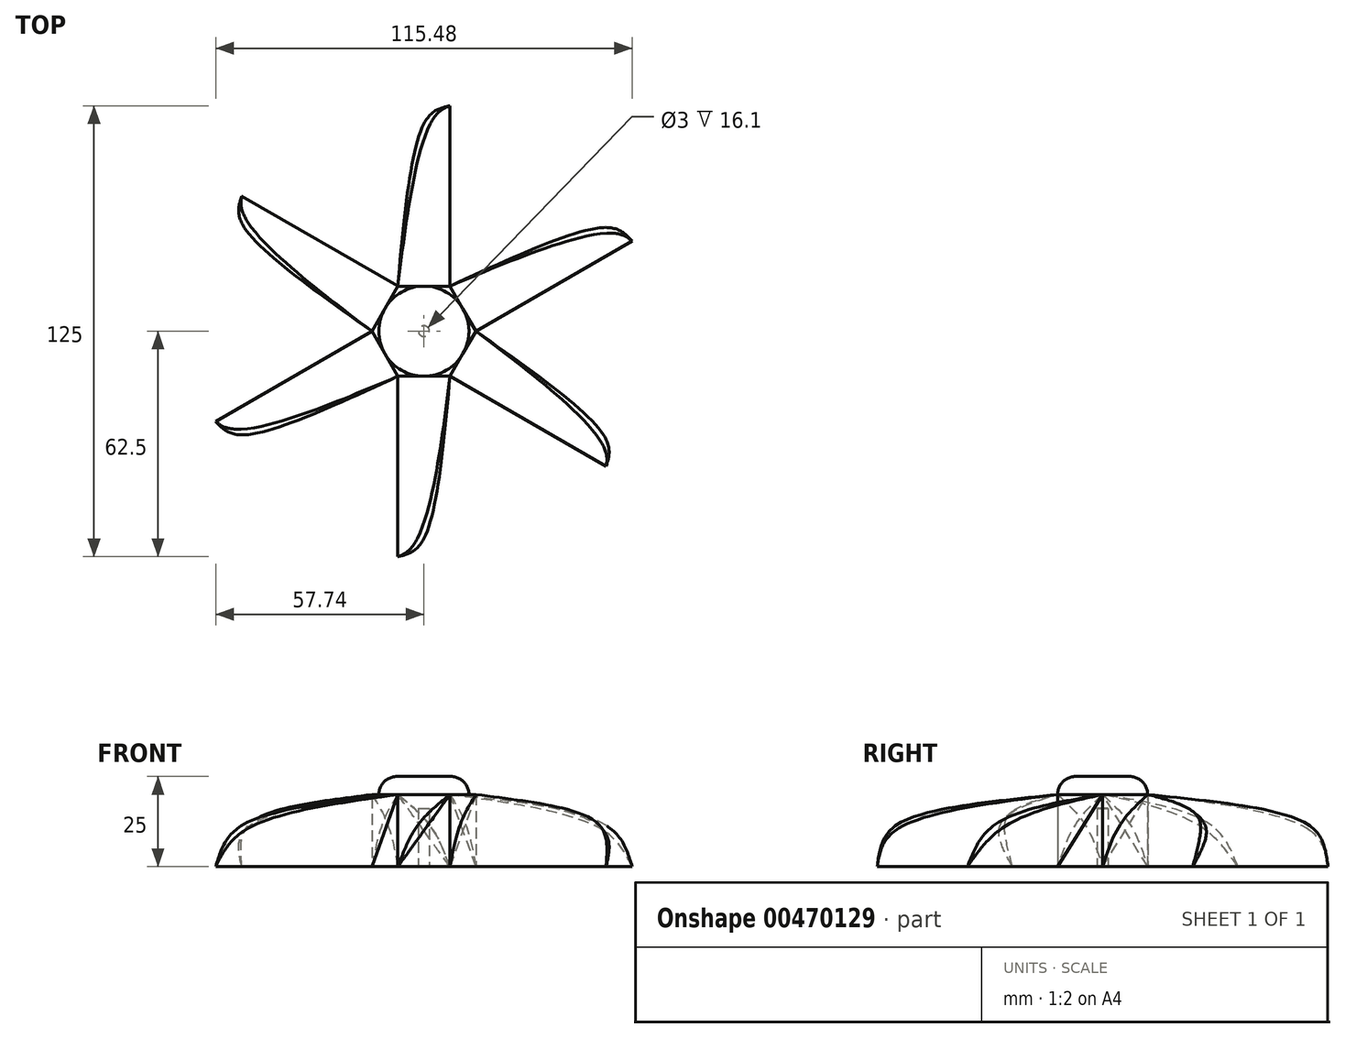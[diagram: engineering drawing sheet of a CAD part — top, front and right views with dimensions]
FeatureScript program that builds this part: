
annotation { "Feature Type Name" : "Feature", "Feature Type Description" : "" }
export const myFeature = defineFeature(function(context is Context, id is Id, definition is map)
    precondition{}
    {
        {
            var Q0;
            Q0=qCreatedBy(makeId("Top.planeOp"),FACE);
            var sketch = newSketch(context, id + "F0", { "sketchPlane" : qUnion([Q0])});
            skCircle(sketch, "E0.cCircle", {"center": v(0, 0) * mm, "radius": 12.5 * mm, "construction": true});
            skLineSegment(sketch, "E0.0", {"start": v(-14.43, 0) * mm, "end": v(-7.22, 12.5) * mm});
            skLineSegment(sketch, "E0.1", {"start": v(-7.22, 12.5) * mm, "end": v(7.22, 12.5) * mm});
            skLineSegment(sketch, "E0.2", {"start": v(7.22, 12.5) * mm, "end": v(14.43, 0) * mm});
            skLineSegment(sketch, "E0.3", {"start": v(14.43, 0) * mm, "end": v(7.22, -12.5) * mm});
            skLineSegment(sketch, "E0.4", {"start": v(7.22, -12.5) * mm, "end": v(-7.22, -12.5) * mm});
            skLineSegment(sketch, "E0.5", {"start": v(-7.22, -12.5) * mm, "end": v(-14.43, 0) * mm});
            skPoint(sketch, "E0.0.midPoint", {"position": v(-10.83, 6.25) * mm});
            skSolve(sketch);
        }
        {
            var Q0;
            Q0=makeQuery(id+"F0.imprint","IMPRINT",FACE,{"disambiguationData":[TD([[makeQuery(id+"F0.imprint","IMPRINT",EDGE,{"derivedFrom":sQuery(id+"F0.wireOp",EDGE,"E0.0")}),-1.0]])]});
            extrude(context, id + "F1", {"entities" : qUnion([Q0]), "depth" : 20 * mm});
        }
        {
            var Q0;
            Q0=makeQuery(id+"F1.opExtrude","SWEPT_FACE",FACE,{"disambiguationData":[OSD([sQuery(id+"F0.wireOp",EDGE,"E0.4")])]});
            var sketch = newSketch(context, id + "F2", { "sketchPlane" : qUnion([Q0])});
            skLineSegment(sketch, "E1", {"start": v(7.22, 20) * mm, "end": v(-7.22, 0) * mm});
            skPoint(sketch, "E2", {"position": v(0, 10) * mm});
            skLineSegment(sketch, "E3", {"start": v(0, 10) * mm, "end": v(-5.73, 14.13) * mm});
            skFitSpline(sketch, "E4", {"points": [v(7.22, 20) * mm, v(-1.82, 11.31) * mm, v(-7.22, 0) * mm], "startDerivative": vector(-19.93, -16.03) * mm, "endDerivative": vector(-8.93, -23.97) * mm});
            skSolve(sketch);
        }
        {
            var Q0;
            {var subQ1=sQuery(id+"F2.wireOp",EDGE,"E1");var subQ4=sQuery(id+"F2.wireOp",EDGE,"E3");var subQ5=makeQuery(id+"F2.imprint","INTERSECT",VERTEX,{"derivedFrom":[subQ1,subQ4]});Q0=makeQuery(id+"F2.imprint","IMPRINT",FACE,{"disambiguationData":[TD([[makeQuery(id+"F2.imprint","IMPRINT",EDGE,{"disambiguationData":[TD([[subQ5,-1.0]])],"derivedFrom":subQ4}),-1.0]])]});}
            var Q1;
            {var subQ1=sQuery(id+"F2.wireOp",EDGE,"E1");var subQ4=sQuery(id+"F2.wireOp",EDGE,"E3");var subQ5=makeQuery(id+"F2.imprint","INTERSECT",VERTEX,{"derivedFrom":[subQ1,subQ4]});Q1=makeQuery(id+"F2.imprint","IMPRINT",FACE,{"disambiguationData":[TD([[makeQuery(id+"F2.imprint","IMPRINT",EDGE,{"disambiguationData":[TD([[subQ5,-1.0]])],"derivedFrom":subQ4}),1.0]])]});}
            extrude(context, id + "F3", {"entities" : qUnion([Q0, Q1]), "operationType" : NewBodyOperationType.ADD, "depth" : 50 * mm});
        }
        {
            var Q0;
            Q0=makeQuery(id+"F1.opExtrude","SWEPT_FACE",FACE,{"disambiguationData":[OSD([sQuery(id+"F0.wireOp",EDGE,"E0.3")])]});
            var sketch = newSketch(context, id + "F4", { "sketchPlane" : qUnion([Q0])});
            skFitSpline(sketch, "E5", {"points": [v(7.22, 20) * mm, v(-1.82, 11.31) * mm, v(-7.22, 0) * mm], "startDerivative": vector(-19.93, -16.03) * mm, "endDerivative": vector(-8.93, -23.97) * mm});
            skLineSegment(sketch, "E6", {"start": v(7.22, 20) * mm, "end": v(-7.22, 0) * mm});
            skSolve(sketch);
        }
        {
            var Q0;
            Q0 = qSketchRegion(id + "F4", true);
            extrude(context, id + "F5", {"entities" : qUnion([Q0]), "operationType" : NewBodyOperationType.ADD, "depth" : 50 * mm});
        }
        {
            var Q0;
            Q0=makeQuery(id+"F1.opExtrude","SWEPT_FACE",FACE,{"disambiguationData":[OSD([sQuery(id+"F0.wireOp",EDGE,"E0.2")])]});
            var sketch = newSketch(context, id + "F6", { "sketchPlane" : qUnion([Q0])});
            skFitSpline(sketch, "E7", {"points": [v(7.22, 20) * mm, v(-1.82, 11.31) * mm, v(-7.22, 0) * mm], "startDerivative": vector(-19.93, -16.03) * mm, "endDerivative": vector(-8.93, -23.97) * mm});
            skLineSegment(sketch, "E8", {"start": v(-7.22, 0) * mm, "end": v(7.22, 20) * mm});
            skSolve(sketch);
        }
        {
            var Q0;
            Q0 = qSketchRegion(id + "F6", true);
            extrude(context, id + "F7", {"entities" : qUnion([Q0]), "operationType" : NewBodyOperationType.ADD, "depth" : 50 * mm});
        }
        {
            var Q0;
            Q0=makeQuery(id+"F1.opExtrude","SWEPT_FACE",FACE,{"disambiguationData":[OSD([sQuery(id+"F0.wireOp",EDGE,"E0.1")])]});
            var sketch = newSketch(context, id + "F8", { "sketchPlane" : qUnion([Q0])});
            skFitSpline(sketch, "E9", {"points": [v(7.25, 20) * mm, v(-1.78, 11.31) * mm, v(-7.18, 0) * mm], "startDerivative": vector(-19.93, -16.03) * mm, "endDerivative": vector(-8.93, -23.97) * mm});
            skLineSegment(sketch, "E10", {"start": v(-7.18, 0) * mm, "end": v(7.25, 20) * mm});
            skSolve(sketch);
        }
        {
            var Q0;
            Q0 = qSketchRegion(id + "F8", true);
            extrude(context, id + "F9", {"entities" : qUnion([Q0]), "operationType" : NewBodyOperationType.ADD, "depth" : 50 * mm});
        }
        {
            var Q0;
            Q0=makeQuery(id+"F1.opExtrude","SWEPT_FACE",FACE,{"disambiguationData":[OSD([sQuery(id+"F0.wireOp",EDGE,"E0.0")])]});
            var sketch = newSketch(context, id + "F10", { "sketchPlane" : qUnion([Q0])});
            skFitSpline(sketch, "E11", {"points": [v(7.22, 20) * mm, v(-1.82, 11.31) * mm, v(-7.22, 0) * mm], "startDerivative": vector(-19.93, -16.03) * mm, "endDerivative": vector(-8.93, -23.97) * mm});
            skLineSegment(sketch, "E12", {"start": v(-7.22, 0) * mm, "end": v(7.22, 20) * mm});
            skSolve(sketch);
        }
        {
            var Q0;
            Q0 = qSketchRegion(id + "F10", true);
            extrude(context, id + "F11", {"entities" : qUnion([Q0]), "operationType" : NewBodyOperationType.ADD, "depth" : 50 * mm});
        }
        {
            var Q0;
            Q0=makeQuery(id+"F1.opExtrude","SWEPT_FACE",FACE,{"disambiguationData":[OSD([sQuery(id+"F0.wireOp",EDGE,"E0.5")])]});
            var sketch = newSketch(context, id + "F12", { "sketchPlane" : qUnion([Q0])});
            skFitSpline(sketch, "E13", {"points": [v(7.22, 20) * mm, v(-1.82, 11.31) * mm, v(-7.22, 0) * mm], "startDerivative": vector(-19.93, -16.03) * mm, "endDerivative": vector(-8.93, -23.97) * mm});
            skLineSegment(sketch, "E14", {"start": v(-7.22, 0) * mm, "end": v(7.22, 20) * mm});
            skSolve(sketch);
        }
        {
            var Q0;
            Q0 = qSketchRegion(id + "F12", true);
            extrude(context, id + "F13", {"entities" : qUnion([Q0]), "operationType" : NewBodyOperationType.ADD, "depth" : 50 * mm});
        }
        {
            var Q0;
            Q0=makeQuery(id+"F13.opExtrude","SWEPT_FACE",FACE,{"disambiguationData":[OSD([sQuery(id+"F12.wireOp",EDGE,"E14")])]});
            var sketch = newSketch(context, id + "F14", { "sketchPlane" : qUnion([Q0])});
            skPoint(sketch, "E15", {"position": v(-56.62, 27.69) * mm});
            skLineSegment(sketch, "E16", {"start": v(-56.62, 27.69) * mm, "end": v(-51.88, 26.09) * mm});
            skFitSpline(sketch, "E17", {"points": [v(-60.56, 16) * mm, v(-51.88, 26.09) * mm, v(-5.3, 23.37) * mm], "startDerivative": vector(16.85, 34.73) * mm, "endDerivative": vector(86.61, -14.97) * mm});
            skSolve(sketch);
        }
        {
            var Q0;
            {var subQ0=sQuery(id+"F14.wireOp",EDGE,"E16");Q0=makeQuery(id+"F14.imprint","IMPRINT",FACE,{"disambiguationData":[TD([[makeQuery(id+"F14.imprint","IMPRINT",EDGE,{"derivedFrom":subQ0}),1.0]])]});}
            var Q1;
            {var subQ0=sQuery(id+"F14.wireOp",EDGE,"E16");Q1=makeQuery(id+"F14.imprint","IMPRINT",FACE,{"disambiguationData":[TD([[makeQuery(id+"F14.imprint","IMPRINT",EDGE,{"derivedFrom":subQ0}),-1.0]])]});}
            extrude(context, id + "F15", {"entities" : qUnion([Q0, Q1]), "operationType" : NewBodyOperationType.REMOVE, "oppositeDirection" : true, "depth" : 25 * mm});
        }
        {
            var Q0;
            Q0=makeQuery(id+"F3.opExtrude","SWEPT_FACE",FACE,{"disambiguationData":[OSD([sQuery(id+"F2.wireOp",EDGE,"E1")])]});
            var sketch = newSketch(context, id + "F16", { "sketchPlane" : qUnion([Q0])});
            skPoint(sketch, "E18", {"position": v(-62.5, 8.1) * mm});
            skLineSegment(sketch, "E19", {"start": v(-62.5, 8.1) * mm, "end": v(-57.5, 8.1) * mm});
            skFitSpline(sketch, "E20", {"points": [v(-62.5, -4.22) * mm, v(-57.5, 8.1) * mm, v(-12.5, 20.44) * mm], "startDerivative": vector(4.85, 38.3) * mm, "endDerivative": vector(86.85, 13.54) * mm});
            skSolve(sketch);
        }
        {
            var Q0;
            {var subQ0=sQuery(id+"F16.wireOp",EDGE,"E19");Q0=makeQuery(id+"F16.imprint","IMPRINT",FACE,{"disambiguationData":[TD([[makeQuery(id+"F16.imprint","IMPRINT",EDGE,{"derivedFrom":subQ0}),1.0]])]});}
            var Q1;
            {var subQ0=sQuery(id+"F16.wireOp",EDGE,"E19");Q1=makeQuery(id+"F16.imprint","IMPRINT",FACE,{"disambiguationData":[TD([[makeQuery(id+"F16.imprint","IMPRINT",EDGE,{"derivedFrom":subQ0}),-1.0]])]});}
            extrude(context, id + "F17", {"entities" : qUnion([Q0, Q1]), "operationType" : NewBodyOperationType.REMOVE, "oppositeDirection" : true, "depth" : 25 * mm});
        }
        {
            var Q0;
            Q0=makeQuery(id+"F5.opExtrude","SWEPT_FACE",FACE,{"disambiguationData":[OSD([sQuery(id+"F4.wireOp",EDGE,"E6")])]});
            var sketch = newSketch(context, id + "F18", { "sketchPlane" : qUnion([Q0])});
            skPoint(sketch, "E21", {"position": v(-61.8, -12.32) * mm});
            skLineSegment(sketch, "E22", {"start": v(-61.8, -12.32) * mm, "end": v(-57.07, -10.72) * mm});
            skFitSpline(sketch, "E23", {"points": [v(-57.86, -24) * mm, v(-57.07, -10.72) * mm, v(-18.39, 15.36) * mm], "startDerivative": vector(-7.67, 37.83) * mm, "endDerivative": vector(77.95, 40.63) * mm});
            skSolve(sketch);
        }
        {
            var Q0;
            {var subQ0=sQuery(id+"F18.wireOp",EDGE,"E22");Q0=makeQuery(id+"F18.imprint","IMPRINT",FACE,{"disambiguationData":[TD([[makeQuery(id+"F18.imprint","IMPRINT",EDGE,{"derivedFrom":subQ0}),1.0]])]});}
            var Q1;
            {var subQ0=sQuery(id+"F18.wireOp",EDGE,"E22");Q1=makeQuery(id+"F18.imprint","IMPRINT",FACE,{"disambiguationData":[TD([[makeQuery(id+"F18.imprint","IMPRINT",EDGE,{"derivedFrom":subQ0}),-1.0]])]});}
            extrude(context, id + "F19", {"entities" : qUnion([Q0, Q1]), "operationType" : NewBodyOperationType.REMOVE, "oppositeDirection" : true, "depth" : 25 * mm});
        }
        {
            var Q0;
            Q0=makeQuery(id+"F7.opExtrude","SWEPT_FACE",FACE,{"disambiguationData":[OSD([sQuery(id+"F6.wireOp",EDGE,"E8")])]});
            var sketch = newSketch(context, id + "F20", { "sketchPlane" : qUnion([Q0])});
            skPoint(sketch, "E24", {"position": v(-56.62, 27.69) * mm});
            skLineSegment(sketch, "E25", {"start": v(-56.62, 27.69) * mm, "end": v(-51.88, 26.09) * mm});
            skFitSpline(sketch, "E26", {"points": [v(-60.56, 16) * mm, v(-51.88, 26.09) * mm, v(-5.3, 23.37) * mm], "startDerivative": vector(16.85, 34.73) * mm, "endDerivative": vector(86.61, -14.97) * mm});
            skSolve(sketch);
        }
        {
            var Q0;
            {var subQ0=sQuery(id+"F20.wireOp",EDGE,"E25");Q0=makeQuery(id+"F20.imprint","IMPRINT",FACE,{"disambiguationData":[TD([[makeQuery(id+"F20.imprint","IMPRINT",EDGE,{"derivedFrom":subQ0}),1.0]])]});}
            var Q1;
            {var subQ0=sQuery(id+"F20.wireOp",EDGE,"E25");Q1=makeQuery(id+"F20.imprint","IMPRINT",FACE,{"disambiguationData":[TD([[makeQuery(id+"F20.imprint","IMPRINT",EDGE,{"derivedFrom":subQ0}),-1.0]])]});}
            extrude(context, id + "F21", {"entities" : qUnion([Q0, Q1]), "operationType" : NewBodyOperationType.REMOVE, "oppositeDirection" : true, "depth" : 25 * mm});
        }
        {
            var Q0;
            Q0=makeQuery(id+"F9.opExtrude","SWEPT_FACE",FACE,{"disambiguationData":[OSD([sQuery(id+"F8.wireOp",EDGE,"E10")])]});
            var sketch = newSketch(context, id + "F22", { "sketchPlane" : qUnion([Q0])});
            skPoint(sketch, "E27", {"position": v(-62.5, 8.13) * mm});
            skLineSegment(sketch, "E28", {"start": v(-62.5, 8.13) * mm, "end": v(-57.5, 8.13) * mm});
            skFitSpline(sketch, "E29", {"points": [v(-62.5, -4.2) * mm, v(-57.5, 8.13) * mm, v(-12.5, 20.46) * mm], "startDerivative": vector(4.85, 38.3) * mm, "endDerivative": vector(86.85, 13.54) * mm});
            skSolve(sketch);
        }
        {
            var Q0;
            {var subQ0=sQuery(id+"F22.wireOp",EDGE,"E28");Q0=makeQuery(id+"F22.imprint","IMPRINT",FACE,{"disambiguationData":[TD([[makeQuery(id+"F22.imprint","IMPRINT",EDGE,{"derivedFrom":subQ0}),1.0]])]});}
            var Q1;
            {var subQ0=sQuery(id+"F22.wireOp",EDGE,"E28");Q1=makeQuery(id+"F22.imprint","IMPRINT",FACE,{"disambiguationData":[TD([[makeQuery(id+"F22.imprint","IMPRINT",EDGE,{"derivedFrom":subQ0}),-1.0]])]});}
            extrude(context, id + "F23", {"entities" : qUnion([Q0, Q1]), "operationType" : NewBodyOperationType.REMOVE, "oppositeDirection" : true, "depth" : 25 * mm});
        }
        {
            var Q0;
            Q0=makeQuery(id+"F11.opExtrude","SWEPT_FACE",FACE,{"disambiguationData":[OSD([sQuery(id+"F10.wireOp",EDGE,"E12")])]});
            var sketch = newSketch(context, id + "F24", { "sketchPlane" : qUnion([Q0])});
            skPoint(sketch, "E30", {"position": v(-61.8, -12.32) * mm});
            skLineSegment(sketch, "E31", {"start": v(-61.8, -12.32) * mm, "end": v(-57.07, -10.72) * mm});
            skFitSpline(sketch, "E32", {"points": [v(-57.86, -24) * mm, v(-57.07, -10.72) * mm, v(-18.39, 15.36) * mm], "startDerivative": vector(-7.67, 37.83) * mm, "endDerivative": vector(77.95, 40.63) * mm});
            skSolve(sketch);
        }
        {
            var Q0;
            {var subQ0=sQuery(id+"F24.wireOp",EDGE,"E31");Q0=makeQuery(id+"F24.imprint","IMPRINT",FACE,{"disambiguationData":[TD([[makeQuery(id+"F24.imprint","IMPRINT",EDGE,{"derivedFrom":subQ0}),1.0]])]});}
            var Q1;
            {var subQ0=sQuery(id+"F24.wireOp",EDGE,"E31");Q1=makeQuery(id+"F24.imprint","IMPRINT",FACE,{"disambiguationData":[TD([[makeQuery(id+"F24.imprint","IMPRINT",EDGE,{"derivedFrom":subQ0}),-1.0]])]});}
            extrude(context, id + "F25", {"entities" : qUnion([Q0, Q1]), "operationType" : NewBodyOperationType.REMOVE, "oppositeDirection" : true, "depth" : 25 * mm});
        }
        {
            var Q0;
            Q0=makeQuery(id+"F1.opExtrude","CAP_FACE",FACE,{"disambiguationData":[OSD([sQuery(id+"F0.wireOp",EDGE,"E0.0"),sQuery(id+"F0.wireOp",EDGE,"E0.1"),sQuery(id+"F0.wireOp",EDGE,"E0.2"),sQuery(id+"F0.wireOp",EDGE,"E0.3"),sQuery(id+"F0.wireOp",EDGE,"E0.4"),sQuery(id+"F0.wireOp",EDGE,"E0.5")])],"isStart":false});
            var sketch = newSketch(context, id + "F26", { "sketchPlane" : qUnion([Q0])});
            skCircle(sketch, "E33", {"center": v(0, 0) * mm, "radius": 12.5 * mm});
            skSolve(sketch);
        }
        {
            var Q0;
            {var subQ0=sQuery(id+"F26.wireOp",EDGE,"E33");var subQ4=makeQuery(id+"F26.imprint","INTERSECT",VERTEX,{"derivedFrom":[makeQuery(id+"F1.opExtrude","CAP_EDGE",EDGE,{"disambiguationData":[OSD([sQuery(id+"F0.wireOp",EDGE,"E0.1")])],"isStart":false}),subQ0]});Q0=makeQuery(id+"F26.imprint","IMPRINT",FACE,{"disambiguationData":[TD([[makeQuery(id+"F26.imprint","IMPRINT",EDGE,{"disambiguationData":[TD([[subQ4,1.0]])],"derivedFrom":subQ0}),1.0]])]});}
            extrude(context, id + "F27", {"entities" : qUnion([Q0]), "operationType" : NewBodyOperationType.ADD, "depth" : 5 * mm});
        }
        {
            var Q0;
            Q0=makeQuery(id+"F27.opExtrude","CAP_EDGE",EDGE,{"disambiguationData":[OSD([sQuery(id+"F26.wireOp",EDGE,"E33")])],"isStart":false});
            fillet(context, id + "F28", {"entities" : qUnion([Q0]), "radius" : 5 * mm, "tangentPropagation" : true, "allowEdgeOverflow" : false});
        }
        {
            var Q0;
            Q0=makeQuery(id+"F1.opExtrude","CAP_FACE",FACE,{"disambiguationData":[OSD([sQuery(id+"F0.wireOp",EDGE,"E0.0"),sQuery(id+"F0.wireOp",EDGE,"E0.1"),sQuery(id+"F0.wireOp",EDGE,"E0.2"),sQuery(id+"F0.wireOp",EDGE,"E0.3"),sQuery(id+"F0.wireOp",EDGE,"E0.4"),sQuery(id+"F0.wireOp",EDGE,"E0.5")])],"isStart":true});
            var sketch = newSketch(context, id + "F29", { "sketchPlane" : qUnion([Q0])});
            skCircle(sketch, "E34", {"center": v(0, 0) * mm, "radius": 1.5 * mm});
            skSolve(sketch);
        }
        {
            var Q0;
            Q0=makeQuery(id+"F29.imprint","IMPRINT",FACE,{"disambiguationData":[TD([[makeQuery(id+"F29.imprint","IMPRINT",EDGE,{"derivedFrom":sQuery(id+"F29.wireOp",EDGE,"E34")}),1.0]])]});
            extrude(context, id + "F30", {"entities" : qUnion([Q0]), "operationType" : NewBodyOperationType.REMOVE, "oppositeDirection" : true, "depth" : 16.1 * mm});
        }
    });
